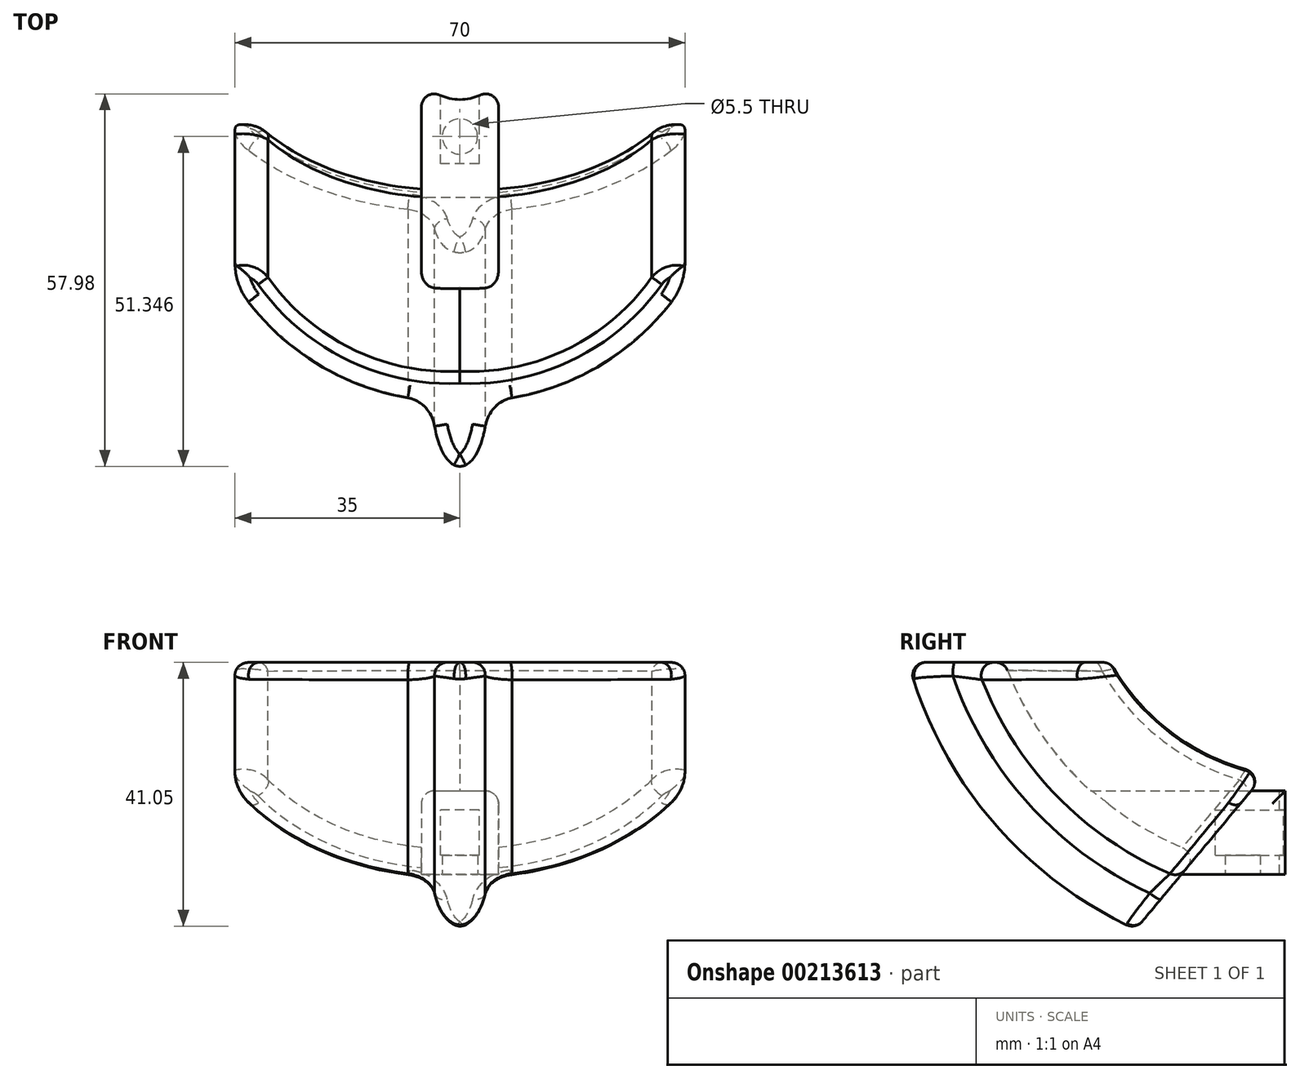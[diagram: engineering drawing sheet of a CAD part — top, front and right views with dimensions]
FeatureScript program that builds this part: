
annotation { "Feature Type Name" : "Feature", "Feature Type Description" : "" }
export const myFeature = defineFeature(function(context is Context, id is Id, definition is map)
    precondition{}
    {
        {
            var Q0;
            Q0=qCreatedBy(makeId("Right.planeOp"),FACE);
            var sketch = newSketch(context, id + "F0", { "sketchPlane" : qUnion([Q0])});
            skLineSegment(sketch, "E0.bottom", {"start": v(0, 0) * mm, "end": v(30, 0) * mm, "construction": true});
            skLineSegment(sketch, "E0.left", {"start": v(0, 0) * mm, "end": v(0, 30) * mm, "construction": true});
            skArc(sketch, "E1", {"start": v(0, 30) * mm, "mid": v(11.66, 11.66) * mm, "end": v(30, 0) * mm});
            skPoint(sketch, "E2", {"position": v(13.08, 10.3) * mm});
            skPoint(sketch, "E3", {"position": v(-15, 30) * mm});
            skPoint(sketch, "E4", {"position": v(3.08, 10.3) * mm});
            skPoint(sketch, "E5", {"position": v(30, 0) * mm});
            skPoint(sketch, "E6", {"position": v(25, 0) * mm});
            skFitSpline(sketch, "E7", {"points": [v(-15, 30) * mm, v(25, 0) * mm, v(100.66, 9.32) * mm], "startDerivative": vector(35.39, -77.1) * mm, "endDerivative": vector(150.07, 40.05) * mm});
            skSolve(sketch);
        }
        {
            var Q0;
            Q0=sQuery(id+"F0.wireOp",VERTEX,"E1.start");
            var Q1;
            Q1=qCreatedBy(makeId("Top.planeOp"),FACE);
            cPlane(context, id + "F1", {"entities" : qUnion([Q0, Q1]), "cplaneType" : CPlaneType.PLANE_POINT, "offset" : 25 * mm, "width" : 150 * mm, "height" : 150 * mm});
        }
        {
            var Q0;
            Q0=qCreatedBy(id+"F1.planeOp",FACE);
            var sketch = newSketch(context, id + "F2", { "sketchPlane" : qUnion([Q0])});
            skArc(sketch, "E8", {"start": v(-35, 24.67) * mm, "mid": v(-21.71, 6.36) * mm, "end": v(0, 0) * mm});
            skArc(sketch, "E9", {"start": v(0, 0) * mm, "mid": v(21.71, 6.36) * mm, "end": v(35, 24.67) * mm});
            skLineSegment(sketch, "E10", {"start": v(-35, 24.67) * mm, "end": v(-35, 16.25) * mm});
            skArc(sketch, "E11.0", {"start": v(0, -5) * mm, "mid": v(18.2, -1.4) * mm, "end": v(32.82, 10.02) * mm});
            skArc(sketch, "E11.1", {"start": v(-32.82, 10.02) * mm, "mid": v(-18.2, -1.4) * mm, "end": v(0, -5) * mm});
            skLineSegment(sketch, "E12", {"start": v(35, 24.67) * mm, "end": v(35, 16.25) * mm});
            skLineSegment(sketch, "E13", {"start": v(0, -5) * mm, "end": v(0, -15) * mm});
            skEllipticalArc(sketch, "E14", {});
            skPoint(sketch, "E15.visualSharp", {"position": v(-35, 13.03) * mm});
            skArc(sketch, "E15.filletArc", {"start": v(-35, 16.25) * mm, "mid": v(-34.44, 12.95) * mm, "end": v(-32.82, 10.02) * mm});
            skPoint(sketch, "E16.visualSharp", {"position": v(35, 13.03) * mm});
            skArc(sketch, "E16.filletArc", {"start": v(32.82, 10.02) * mm, "mid": v(34.44, 12.95) * mm, "end": v(35, 16.25) * mm});
            const initialGuessF2  = {"E14": [0, -0.005004295268239853, 0, -1, 0.01, 0.00424685629998106, 4.184836836168355, 2.098348471011326]};
            skSetInitialGuess(sketch, initialGuessF2);
            skSolve(sketch);
        }
        {
            var Q0;
            Q0=sQuery(id+"F0.wireOp",VERTEX,"E2");
            var Q1;
            Q1=qCreatedBy(makeId("Top.planeOp"),FACE);
            cPlane(context, id + "F3", {"entities" : qUnion([Q0, Q1]), "cplaneType" : CPlaneType.PLANE_POINT, "offset" : 25 * mm, "width" : 150 * mm, "height" : 150 * mm});
        }
        {
            var Q0;
            {var subQ5=sQuery(id+"F2.wireOp",EDGE,"E10");Q0=makeQuery(id+"F2.imprint","IMPRINT",FACE,{"disambiguationData":[TD([[makeQuery(id+"F2.imprint","IMPRINT",EDGE,{"derivedFrom":subQ5}),1.0]])]});}
            var Q1;
            {var subQ6=sQuery(id+"F2.wireOp",EDGE,"E9");var subQ7=sQuery(id+"F2.wireOp",EDGE,"E8");var subQ8=makeQuery(id+"F2.imprint","INTERSECT",VERTEX,{"derivedFrom":[subQ7,subQ6]});Q1=makeQuery(id+"F2.imprint","IMPRINT",FACE,{"disambiguationData":[TD([[makeQuery(id+"F2.imprint","IMPRINT",EDGE,{"disambiguationData":[TD([[subQ8,1.0]])],"derivedFrom":subQ7}),-1.0]])]});}
            var Q2;
            {var subQ5=sQuery(id+"F2.wireOp",EDGE,"E12");Q2=makeQuery(id+"F2.imprint","IMPRINT",FACE,{"disambiguationData":[TD([[makeQuery(id+"F2.imprint","IMPRINT",EDGE,{"derivedFrom":subQ5}),-1.0]])]});}
            var Q3;
            {var subQ0=sQuery(id+"F2.wireOp",EDGE,"E13");Q3=makeQuery(id+"F2.imprint","IMPRINT",FACE,{"disambiguationData":[TD([[makeQuery(id+"F2.imprint","IMPRINT",EDGE,{"derivedFrom":subQ0}),1.0]])]});}
            var Q4;
            {var subQ0=sQuery(id+"F2.wireOp",EDGE,"E13");Q4=makeQuery(id+"F2.imprint","IMPRINT",FACE,{"disambiguationData":[TD([[makeQuery(id+"F2.imprint","IMPRINT",EDGE,{"derivedFrom":subQ0}),-1.0]])]});}
            var Q5;
            Q5=sQuery(id+"F0.wireOp",EDGE,"E1");
            sweep(context, id + "F4", {"profiles" : qUnion([Q0, Q1, Q2, Q3, Q4]), "path" : qUnion([Q5])});
        }
        {
            var Q0;
            Q0=qCreatedBy(makeId("Front.planeOp"),FACE);
            var Q1;
            Q1=makeQuery(id+"F4.opSweep","CAP_VERTEX",VERTEX,{"disambiguationData":[OSD([sQuery(id+"F0.wireOp",EDGE,"E1"),sQuery(id+"F2.wireOp",EDGE,"E9"),sQuery(id+"F2.wireOp",EDGE,"E12")])],"isStart":false});
            cPlane(context, id + "F5", {"entities" : qUnion([Q0, Q1]), "cplaneType" : CPlaneType.PLANE_POINT, "offset" : 25 * mm, "width" : 150 * mm, "height" : 150 * mm});
        }
        {
            var Q0;
            Q0=qCreatedBy(id+"F5.planeOp",FACE);
            var sketch = newSketch(context, id + "F6", { "sketchPlane" : qUnion([Q0])});
            skLineSegment(sketch, "E17.bottom", {"start": v(3, 0) * mm, "end": v(-3, 0) * mm});
            skLineSegment(sketch, "E17.top", {"start": v(3, 7) * mm, "end": v(-3, 7) * mm});
            skLineSegment(sketch, "E17.left", {"start": v(3, 0) * mm, "end": v(3, 7) * mm});
            skLineSegment(sketch, "E17.right", {"start": v(-3, 0) * mm, "end": v(-3, 7) * mm});
            skPoint(sketch, "E17.middle", {"position": v(0, 3.5) * mm});
            skLineSegment(sketch, "E18.0", {"start": v(6, 10) * mm, "end": v(-6, 10) * mm});
            skLineSegment(sketch, "E18.1", {"start": v(6, -3) * mm, "end": v(6, 10) * mm});
            skLineSegment(sketch, "E18.2", {"start": v(6, -3) * mm, "end": v(-6, -3) * mm});
            skLineSegment(sketch, "E18.3", {"start": v(-6, -3) * mm, "end": v(-6, 10) * mm});
            skSolve(sketch);
        }
        {
            var Q0;
            Q0=makeQuery(id+"F6.imprint","IMPRINT",FACE,{"disambiguationData":[TD([[makeQuery(id+"F6.imprint","IMPRINT",EDGE,{"derivedFrom":sQuery(id+"F6.wireOp",EDGE,"E17.bottom")}),1.0]])]});
            var Q1;
            Q1=makeQuery(id+"F6.imprint","IMPRINT",FACE,{"disambiguationData":[TD([[makeQuery(id+"F6.imprint","IMPRINT",EDGE,{"derivedFrom":sQuery(id+"F6.wireOp",EDGE,"E17.bottom")}),-1.0]])]});
            extrude(context, id + "F7", {"entities" : qUnion([Q0, Q1]), "operationType" : NewBodyOperationType.ADD, "endBound" : BoundingType.UP_TO_NEXT, "depth" : 25 * mm});
        }
        {
            var Q0;
            Q0=makeQuery(id+"F6.imprint","IMPRINT",FACE,{"disambiguationData":[TD([[makeQuery(id+"F6.imprint","IMPRINT",EDGE,{"derivedFrom":sQuery(id+"F6.wireOp",EDGE,"E17.bottom")}),-1.0]])]});
            extrude(context, id + "F8", {"entities" : qUnion([Q0]), "operationType" : NewBodyOperationType.REMOVE, "depth" : 13 * mm});
        }
        {
            var Q0;
            Q0=makeQuery(id+"F7.opExtrude","SWEPT_FACE",FACE,{"disambiguationData":[OSD([sQuery(id+"F6.wireOp",EDGE,"E18.0")])]});
            var sketch = newSketch(context, id + "F9", { "sketchPlane" : qUnion([Q0])});
            skArc(sketch, "E19", {"start": v(-6, 45.79) * mm, "mid": v(0, 42.79) * mm, "end": v(6, 45.79) * mm});
            skLineSegment(sketch, "E20", {"start": v(-6, 45.79) * mm, "end": v(6, 45.79) * mm});
            skSolve(sketch);
        }
        {
            var Q0;
            Q0 = qSketchRegion(id + "F9", true);
            extrude(context, id + "F10", {"entities" : qUnion([Q0]), "operationType" : NewBodyOperationType.REMOVE, "endBound" : BoundingType.THROUGH_ALL, "oppositeDirection" : true, "depth" : 25 * mm});
        }
        {
            var Q0;
            Q0=makeQuery(id+"F4.opSweep","SWEPT_EDGE",EDGE,{"disambiguationData":[OSD([sQuery(id+"F0.wireOp",EDGE,"E1"),sQuery(id+"F2.wireOp",EDGE,"E8"),sQuery(id+"F2.wireOp",EDGE,"E10")])]});
            var Q1;
            Q1=makeQuery(id+"F4.opSweep","SWEPT_EDGE",EDGE,{"disambiguationData":[OSD([sQuery(id+"F0.wireOp",EDGE,"E1"),sQuery(id+"F2.wireOp",EDGE,"E9"),sQuery(id+"F2.wireOp",EDGE,"E12")])]});
            var Q2;
            Q2=makeQuery(id+"F4.opSweep","SWEPT_EDGE",EDGE,{"disambiguationData":[OSD([sQuery(id+"F0.wireOp",EDGE,"E1"),sQuery(id+"F2.wireOp",EDGE,"E11.1"),sQuery(id+"F2.wireOp",EDGE,"E14")])]});
            var Q3;
            Q3=makeQuery(id+"F4.opSweep","SWEPT_EDGE",EDGE,{"disambiguationData":[OSD([sQuery(id+"F0.wireOp",EDGE,"E1"),sQuery(id+"F2.wireOp",EDGE,"E11.0"),sQuery(id+"F2.wireOp",EDGE,"E14")])]});
            fillet(context, id + "F11", {"entities" : qUnion([Q0, Q1, Q2, Q3]), "radius" : 5 * mm, "tangentPropagation" : true, "allowEdgeOverflow" : false});
        }
        {
            var Q0;
            Q0=makeQuery(id+"F4.opSweep","CAP_EDGE",EDGE,{"disambiguationData":[OSD([sQuery(id+"F0.wireOp",VERTEX,"E1.end"),sQuery(id+"F2.wireOp",EDGE,"E8")])],"isStart":false});
            var Q1;
            Q1=makeQuery(id+"F4.opSweep","CAP_EDGE",EDGE,{"disambiguationData":[OSD([sQuery(id+"F0.wireOp",VERTEX,"E1.end"),sQuery(id+"F2.wireOp",EDGE,"E9")])],"isStart":false});
            var Q2;
            Q2=makeQuery(id+"F4.opSweep","CAP_EDGE",EDGE,{"disambiguationData":[OSD([sQuery(id+"F0.wireOp",VERTEX,"E1.end"),sQuery(id+"F2.wireOp",EDGE,"E11.1")])],"isStart":false});
            var Q3;
            Q3=makeQuery(id+"F4.opSweep","CAP_FACE",FACE,{"disambiguationData":[OSD([sQuery(id+"F0.wireOp",VERTEX,"E1.start"),sQuery(id+"F2.wireOp",EDGE,"E8"),sQuery(id+"F2.wireOp",EDGE,"E9"),sQuery(id+"F2.wireOp",EDGE,"E10"),sQuery(id+"F2.wireOp",EDGE,"E11.0"),sQuery(id+"F2.wireOp",EDGE,"E11.1"),sQuery(id+"F2.wireOp",EDGE,"E12"),sQuery(id+"F2.wireOp",EDGE,"E14"),sQuery(id+"F2.wireOp",EDGE,"E15.filletArc"),sQuery(id+"F2.wireOp",EDGE,"E16.filletArc")])],"isStart":true});
            var Q4;
            Q4=makeQuery(id+"F7.opExtrude","SWEPT_EDGE",EDGE,{"disambiguationData":[OSD([sQuery(id+"F6.wireOp",EDGE,"E18.0"),sQuery(id+"F6.wireOp",EDGE,"E18.1")])]});
            var Q5;
            Q5=makeQuery(id+"F7.opExtrude","SWEPT_EDGE",EDGE,{"disambiguationData":[OSD([sQuery(id+"F6.wireOp",EDGE,"E18.0"),sQuery(id+"F6.wireOp",EDGE,"E18.3")])]});
            var Q6;
            {var subQ0=sQuery(id+"F6.wireOp",EDGE,"E18.1");Q6=makeQuery(id+"F10.boolean.opBoolean","MERGE",EDGE,{"derivedFrom":[makeQuery(id+"F7.opExtrude","CAP_EDGE",EDGE,{"disambiguationData":[OSD([subQ0])],"isStart":true}),makeQuery(id+"F10.opExtrude","SWEPT_EDGE",EDGE,{"disambiguationData":[OSD([sQuery(id+"F6.wireOp",EDGE,"E18.0"),subQ0,sQuery(id+"F9.wireOp",EDGE,"E19"),sQuery(id+"F9.wireOp",EDGE,"E20")])]})]});}
            var Q7;
            {var subQ0=sQuery(id+"F6.wireOp",EDGE,"E18.3");Q7=makeQuery(id+"F10.boolean.opBoolean","MERGE",EDGE,{"derivedFrom":[makeQuery(id+"F7.opExtrude","CAP_EDGE",EDGE,{"disambiguationData":[OSD([subQ0])],"isStart":true}),makeQuery(id+"F10.opExtrude","SWEPT_EDGE",EDGE,{"disambiguationData":[OSD([sQuery(id+"F6.wireOp",EDGE,"E18.0"),subQ0,sQuery(id+"F9.wireOp",EDGE,"E19"),sQuery(id+"F9.wireOp",EDGE,"E20")])]})]});}
            fillet(context, id + "F12", {"entities" : qUnion([Q0, Q1, Q2, Q3, Q4, Q5, Q6, Q7]), "radius" : 2 * mm, "tangentPropagation" : true, "allowEdgeOverflow" : false});
        }
        {
            var Q0;
            Q0=makeQuery(id+"F7.opExtrude","SWEPT_FACE",FACE,{"disambiguationData":[OSD([sQuery(id+"F6.wireOp",EDGE,"E18.2")])]});
            var sketch = newSketch(context, id + "F13", { "sketchPlane" : qUnion([Q0])});
            skCircle(sketch, "E21", {"center": v(0, -37.04) * mm, "radius": 2.75 * mm});
            skPoint(sketch, "E21.centerSnap0", {"position": v(0, -42.79) * mm});
            skSolve(sketch);
        }
        {
            var Q0;
            Q0 = qSketchRegion(id + "F13", true);
            extrude(context, id + "F14", {"entities" : qUnion([Q0]), "operationType" : NewBodyOperationType.REMOVE, "endBound" : BoundingType.UP_TO_NEXT, "oppositeDirection" : true, "depth" : 25 * mm});
        }
    });
